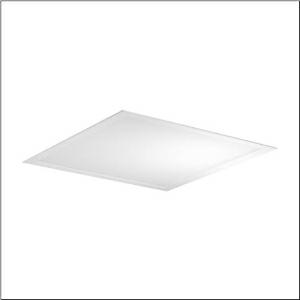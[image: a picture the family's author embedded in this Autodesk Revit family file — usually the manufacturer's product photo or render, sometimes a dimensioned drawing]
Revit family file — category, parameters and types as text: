
# Revit family: apollon_21_square_51mq11wd2m14
name_source: partatom
category: Lighting Fixtures
units: mm (PartAtom-declared; Revit-internal decimal feet)

## family parameters
Cut with Voids When Loaded = No
Host = Face
Light Source = No
Part Type = Normal
Room Calculation Point = No
Round Connector Dimension = Use Diameter
Shared = No

## types (1)
- --- (1 x LED, 4200 lm, 26 W, 4000K)
    Apparent Load = 26 VA
    CIE Flux Codes = 60 87 97 100 100
    Color Rendering = 80
    Color Temperature = 4000K
    Default Elevation = 1800 mm
    Description = Apollon 21 square, office luminaire, primary optical cover: micro prismatic cover, of PMMA, CAT 2 (L<= 3000cd/m²), light emission: direct distribution, primary light characteristic: symmetric, installation type: lay-in mounting, recessed, LED, rated luminous flux: 4.200lm, luminous efficacy: 162lm/W, light colour: 830/840, colour temperature: 3000/4000K, control gear: DALI 2, Multilumen, with terminal, 5-pole, mains connection: 220..240V, AC/DC, 0/50..60Hz, rated input power: 26W, suitable for self-contained emergency lighting element 59MQE002602A with integrated self-test function according to EN 60598-2-22, housing, of aluminium, coated, traffic white (RAL 9016), module: M625, length: 620mm, width: 620mm, height: 55mm, housing upper side, of sheet steel, galvanised, protection rating (complete): IP20, protection rating (lamp compartment, on room side): IP50, insulation class (complete): insulation class II (safety insulation), certification: CE, ENEC, UKCA, impact resistance: IK03, permissible operating ambient temperature: -20..+45°C, standard: EN 60598-2-22, corresponds to IFS (International Featured Standards) requirements for safety and quality in the food industry, packaging unit: 1 piece
    Height = 0 mm  [stored 0 ft]
    Lamp = 1 x LED
    Lamp Light Flux = 4200 lm
    Lamp Power = 26 W
    Lamp count = 1
    Length = 620 mm
    Luminous efficacy = 162 lm/W
    Manufacturer = Siteco
    ModVariant = No
    Model = 51MQ11WD2M14
    Mounting Place = Ceiling
    Mounting Type = Recessed
    Number of Poles = 1
    OnlyDefault = Yes
    Power Factor = 1
    Product Name = Apollon 21 square
    Product group = office luminaire | ceiling recessed
    ProductGroupID = 400
    Protection Class = Protection class II
    Protection Degree = IP 20
    RLX_Detail_Level = 1
    RLX_Emergency_Light_Flux = 0 lm
    RLX_Emergency_Type = 0
    RLX_Emergency_Type_DB = No
    RlxData = <blob elided: 13485 chars, md5=27005292>
    Socket = socket
    Standby Power = 0 W
    System Light Flux = 4200 lm
    System Power = 26 W
    Type Comments = factory setting
    Type Image = l_1291054.jpg
    URL = http://relux.com
    VarID = @adj_075921
    Voltage = 0 V
    Weight = 0.00 kg
    Width = 620 mm

note: [stored X ft] marks values corroborated as IEEE doubles in the binary element streams (Revit-internal decimal feet)

## geometry (parser evidence)
native form markers: Sweep x10
no freeform markers — native parametric forms only
